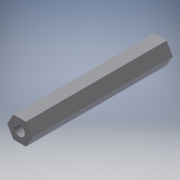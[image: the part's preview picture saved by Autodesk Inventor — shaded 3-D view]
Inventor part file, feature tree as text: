
AUTODESK INVENTOR PART (.ipt)
format: ipt  version: 2016 (Build 200138000, 138)  size: 108,544 bytes
history: native  units: in
note: dims shown in document units (in); Inventor stores cm internally (conversion verified against a paired STEP export)
features: other x1, imported_body x1, extrude x1, sketch x1
ambient origin geometry x8: Origin, YZ Plane, XZ Plane, XY Plane, X Axis, Y Axis, Z Axis, Center Point
bodies: Body1 (feature_tree)
feature tree (4):
  other  "STANDOFF_2_INCH_2011"
  imported_body  "Base1"
  extrude  "Extrusion1"  [1 undecoded]
  sketch  "Sketch1"  dims[d0=0.4in d1=0.0in]
note: 1 required parameter value undecoded (feature->parameter linkage not recoverable at this tier; creation-order binding heuristic only, values carry confidence <= 0.55)
